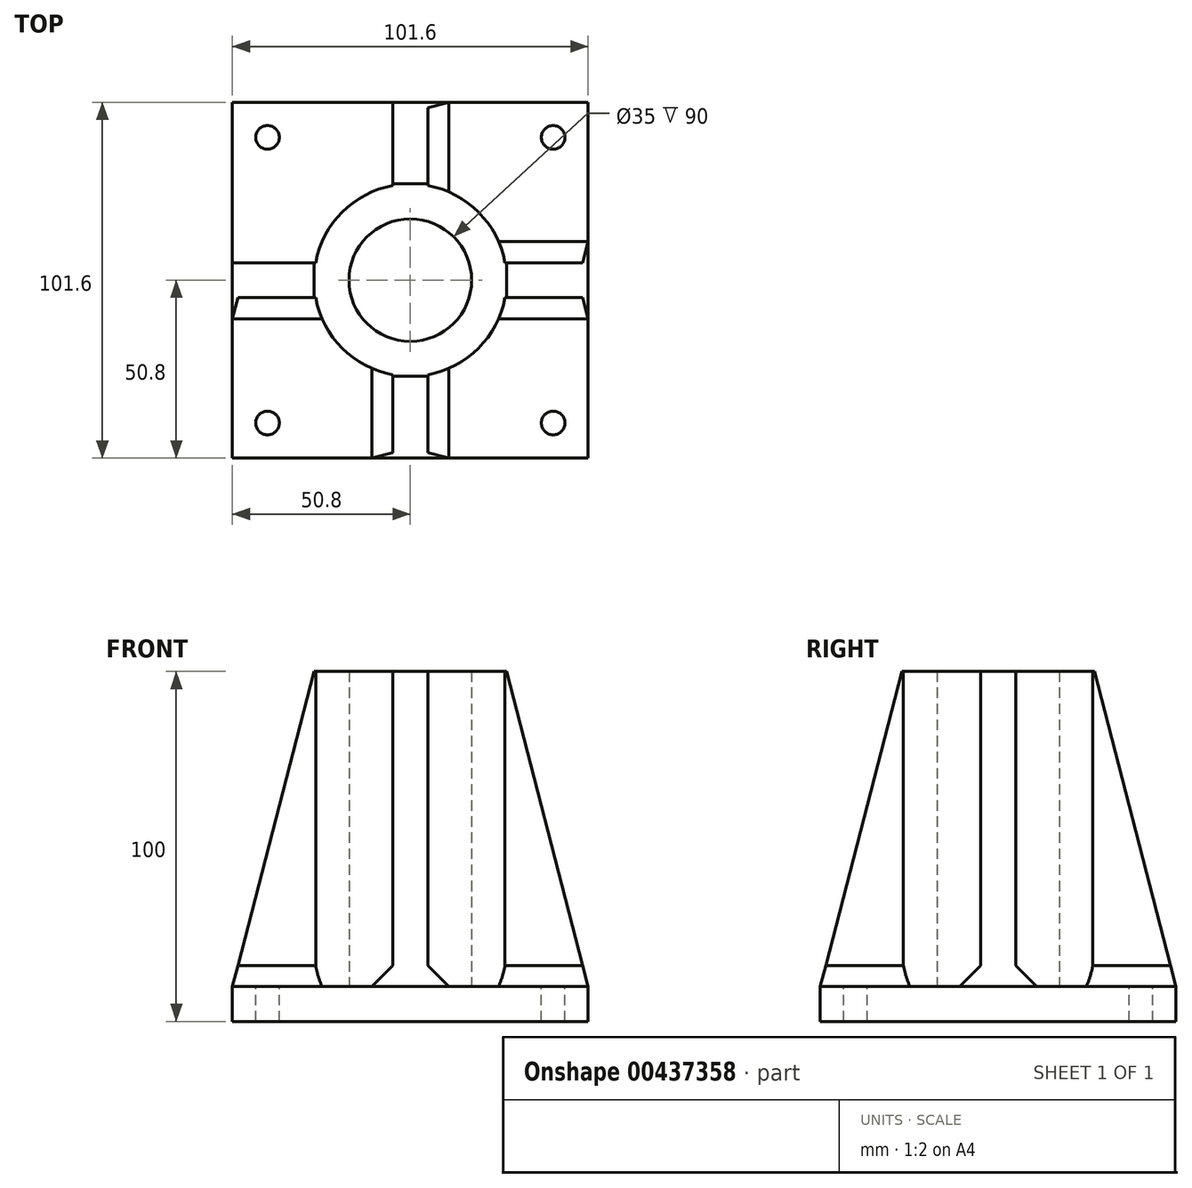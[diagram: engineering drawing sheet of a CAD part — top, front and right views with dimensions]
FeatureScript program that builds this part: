
annotation { "Feature Type Name" : "Feature", "Feature Type Description" : "" }
export const myFeature = defineFeature(function(context is Context, id is Id, definition is map)
    precondition{}
    {
        {
            assignVariable(context, id + "F0", {"name" : "PrintingOffset", "anyValue" : .5});
        }
        {
            assignVariable(context, id + "F1", {"name" : "BoltHoleDiameter", "anyValue" : 6.25 + getVariable(context, 'PrintingOffset')});
        }
        {
            assignVariable(context, id + "F2", {"name" : "PlateLength", "anyValue" : 101.6});
        }
        {
            assignVariable(context, id + "F3", {"name" : "PlateWidth", "anyValue" : getVariable(context, 'PlateLength')});
        }
        {
            assignVariable(context, id + "F4", {"name" : "TableLegDiameter", "anyValue" : 34.5 + getVariable(context, 'PrintingOffset')});
        }
        {
            assignVariable(context, id + "F5", {"name" : "WallThickness", "anyValue" : 10});
        }
        {
            var Q0;
            Q0=qCreatedBy(makeId("Top.planeOp"),FACE);
            var sketch = newSketch(context, id + "F6", { "sketchPlane" : qUnion([Q0])});
            skLineSegment(sketch, "E0.rect.bottom", {"start": v(50.8, 50.8) * mm, "end": v(-50.8, 50.8) * mm});
            skLineSegment(sketch, "E0.rect.top", {"start": v(50.8, -50.8) * mm, "end": v(-50.8, -50.8) * mm});
            skLineSegment(sketch, "E0.rect.left", {"start": v(50.8, 50.8) * mm, "end": v(50.8, -50.8) * mm});
            skLineSegment(sketch, "E0.rect.right", {"start": v(-50.8, 50.8) * mm, "end": v(-50.8, -50.8) * mm});
            skPoint(sketch, "E0.rect.middle", {"position": v(0, 0) * mm});
            skCircle(sketch, "E1", {"center": v(0, 0) * mm, "radius": 17.5 * mm});
            skLineSegment(sketch, "E2", {"start": v(0, 50.8) * mm, "end": v(0, -50.8) * mm, "construction": true});
            skLineSegment(sketch, "E3", {"start": v(-50.8, 0) * mm, "end": v(50.8, 0) * mm, "construction": true});
            skCircle(sketch, "E4.0", {"center": v(0, 0) * mm, "radius": 27.5 * mm});
            skLineSegment(sketch, "E5.3.0", {"start": v(-27.04, 5) * mm, "end": v(-50.8, 5) * mm});
            skLineSegment(sketch, "E5.3.1", {"start": v(-27.04, -5) * mm, "end": v(-50.8, -5) * mm});
            skPoint(sketch, "E6", {"position": v(-40.8, 40.8) * mm});
            skLineSegment(sketch, "E7", {"start": v(0, -17.5) * mm, "end": v(0, -17.5) * mm});
            skLineSegment(sketch, "E8.1.0", {"start": v(1.46, -17.44) * mm, "end": v(1.46, -17.44) * mm});
            skLineSegment(sketch, "E8.2.0", {"start": v(2.92, -17.25) * mm, "end": v(2.92, -17.25) * mm});
            skLineSegment(sketch, "E8.3.0", {"start": v(4.35, -16.95) * mm, "end": v(4.35, -16.95) * mm});
            skLineSegment(sketch, "E8.4.0", {"start": v(5.76, -16.53) * mm, "end": v(5.76, -16.53) * mm});
            skLineSegment(sketch, "E8.5.0", {"start": v(7.12, -15.99) * mm, "end": v(7.12, -15.99) * mm});
            skLineSegment(sketch, "E8.6.0", {"start": v(8.43, -15.34) * mm, "end": v(8.43, -15.34) * mm});
            skLineSegment(sketch, "E8.7.0", {"start": v(9.68, -14.58) * mm, "end": v(9.68, -14.58) * mm});
            skLineSegment(sketch, "E8.8.0", {"start": v(10.87, -13.71) * mm, "end": v(10.87, -13.71) * mm});
            skLineSegment(sketch, "E8.9.0", {"start": v(11.98, -12.76) * mm, "end": v(11.98, -12.76) * mm});
            skLineSegment(sketch, "E8.10.0", {"start": v(13, -11.7) * mm, "end": v(13, -11.7) * mm});
            skLineSegment(sketch, "E8.11.0", {"start": v(13.94, -10.58) * mm, "end": v(13.94, -10.58) * mm});
            skLineSegment(sketch, "E8.12.0", {"start": v(14.78, -9.38) * mm, "end": v(14.78, -9.38) * mm});
            skLineSegment(sketch, "E8.13.0", {"start": v(15.5, -8.1) * mm, "end": v(15.5, -8.1) * mm});
            skLineSegment(sketch, "E8.14.0", {"start": v(16.13, -6.78) * mm, "end": v(16.13, -6.78) * mm});
            skLineSegment(sketch, "E8.15.0", {"start": v(16.64, -5.4) * mm, "end": v(16.64, -5.4) * mm});
            skLineSegment(sketch, "E8.16.0", {"start": v(17.04, -4) * mm, "end": v(17.04, -4) * mm});
            skLineSegment(sketch, "E8.17.0", {"start": v(17.31, -2.56) * mm, "end": v(17.31, -2.56) * mm});
            skLineSegment(sketch, "E8.18.0", {"start": v(17.47, -1.1) * mm, "end": v(17.47, -1.1) * mm});
            skLineSegment(sketch, "E8.19.0", {"start": v(17.5, 0.37) * mm, "end": v(17.5, 0.37) * mm});
            skLineSegment(sketch, "E8.20.0", {"start": v(17.4, 1.83) * mm, "end": v(17.4, 1.83) * mm});
            skLineSegment(sketch, "E8.21.0", {"start": v(17.2, 3.28) * mm, "end": v(17.2, 3.28) * mm});
            skLineSegment(sketch, "E8.22.0", {"start": v(16.86, 4.7) * mm, "end": v(16.86, 4.7) * mm});
            skLineSegment(sketch, "E8.23.0", {"start": v(16.4, 6.1) * mm, "end": v(16.4, 6.1) * mm});
            skLineSegment(sketch, "E8.24.0", {"start": v(15.83, 7.45) * mm, "end": v(15.83, 7.45) * mm});
            skLineSegment(sketch, "E8.25.0", {"start": v(15.16, 8.75) * mm, "end": v(15.16, 8.75) * mm});
            skLineSegment(sketch, "E8.26.0", {"start": v(14.37, 9.99) * mm, "end": v(14.37, 9.99) * mm});
            skLineSegment(sketch, "E8.27.0", {"start": v(13.48, 11.15) * mm, "end": v(13.48, 11.15) * mm});
            skLineSegment(sketch, "E8.28.0", {"start": v(12.5, 12.24) * mm, "end": v(12.5, 12.24) * mm});
            skLineSegment(sketch, "E8.29.0", {"start": v(11.43, 13.25) * mm, "end": v(11.43, 13.25) * mm});
            skLineSegment(sketch, "E8.30.0", {"start": v(10.29, 14.16) * mm, "end": v(10.29, 14.16) * mm});
            skLineSegment(sketch, "E8.31.0", {"start": v(9.07, 14.97) * mm, "end": v(9.07, 14.97) * mm});
            skLineSegment(sketch, "E8.32.0", {"start": v(7.78, 15.67) * mm, "end": v(7.78, 15.67) * mm});
            skLineSegment(sketch, "E8.33.0", {"start": v(6.44, 16.27) * mm, "end": v(6.44, 16.27) * mm});
            skLineSegment(sketch, "E8.34.0", {"start": v(5.06, 16.75) * mm, "end": v(5.06, 16.75) * mm});
            skLineSegment(sketch, "E8.35.0", {"start": v(3.64, 17.12) * mm, "end": v(3.64, 17.12) * mm});
            skLineSegment(sketch, "E8.36.0", {"start": v(2.2, 17.36) * mm, "end": v(2.2, 17.36) * mm});
            skLineSegment(sketch, "E8.37.0", {"start": v(0.73, 17.48) * mm, "end": v(0.73, 17.48) * mm});
            skLineSegment(sketch, "E8.38.0", {"start": v(-0.73, 17.48) * mm, "end": v(-0.73, 17.48) * mm});
            skLineSegment(sketch, "E8.39.0", {"start": v(-2.2, 17.36) * mm, "end": v(-2.2, 17.36) * mm});
            skLineSegment(sketch, "E8.40.0", {"start": v(-3.64, 17.12) * mm, "end": v(-3.64, 17.12) * mm});
            skLineSegment(sketch, "E8.41.0", {"start": v(-5.06, 16.75) * mm, "end": v(-5.06, 16.75) * mm});
            skLineSegment(sketch, "E8.42.0", {"start": v(-6.44, 16.27) * mm, "end": v(-6.44, 16.27) * mm});
            skLineSegment(sketch, "E8.43.0", {"start": v(-7.78, 15.67) * mm, "end": v(-7.78, 15.67) * mm});
            skLineSegment(sketch, "E8.44.0", {"start": v(-9.07, 14.97) * mm, "end": v(-9.07, 14.97) * mm});
            skLineSegment(sketch, "E8.45.0", {"start": v(-10.29, 14.16) * mm, "end": v(-10.29, 14.16) * mm});
            skLineSegment(sketch, "E8.46.0", {"start": v(-11.43, 13.25) * mm, "end": v(-11.43, 13.25) * mm});
            skLineSegment(sketch, "E8.47.0", {"start": v(-12.5, 12.24) * mm, "end": v(-12.5, 12.24) * mm});
            skLineSegment(sketch, "E8.48.0", {"start": v(-13.48, 11.15) * mm, "end": v(-13.48, 11.15) * mm});
            skLineSegment(sketch, "E8.49.0", {"start": v(-14.37, 9.99) * mm, "end": v(-14.37, 9.99) * mm});
            skLineSegment(sketch, "E8.50.0", {"start": v(-15.16, 8.75) * mm, "end": v(-15.16, 8.75) * mm});
            skLineSegment(sketch, "E8.51.0", {"start": v(-15.83, 7.45) * mm, "end": v(-15.83, 7.45) * mm});
            skLineSegment(sketch, "E8.52.0", {"start": v(-16.4, 6.1) * mm, "end": v(-16.4, 6.1) * mm});
            skLineSegment(sketch, "E8.53.0", {"start": v(-16.86, 4.7) * mm, "end": v(-16.86, 4.7) * mm});
            skLineSegment(sketch, "E8.54.0", {"start": v(-17.2, 3.28) * mm, "end": v(-17.2, 3.28) * mm});
            skLineSegment(sketch, "E8.55.0", {"start": v(-17.4, 1.83) * mm, "end": v(-17.4, 1.83) * mm});
            skLineSegment(sketch, "E8.56.0", {"start": v(-17.5, 0.37) * mm, "end": v(-17.5, 0.37) * mm});
            skLineSegment(sketch, "E8.57.0", {"start": v(-17.47, -1.1) * mm, "end": v(-17.47, -1.1) * mm});
            skLineSegment(sketch, "E8.58.0", {"start": v(-17.31, -2.56) * mm, "end": v(-17.31, -2.56) * mm});
            skLineSegment(sketch, "E8.59.0", {"start": v(-17.04, -4) * mm, "end": v(-17.04, -4) * mm});
            skLineSegment(sketch, "E8.60.0", {"start": v(-16.64, -5.4) * mm, "end": v(-16.64, -5.4) * mm});
            skLineSegment(sketch, "E8.61.0", {"start": v(-16.13, -6.78) * mm, "end": v(-16.13, -6.78) * mm});
            skLineSegment(sketch, "E8.62.0", {"start": v(-15.5, -8.1) * mm, "end": v(-15.5, -8.1) * mm});
            skLineSegment(sketch, "E8.63.0", {"start": v(-14.78, -9.38) * mm, "end": v(-14.78, -9.38) * mm});
            skLineSegment(sketch, "E8.64.0", {"start": v(-13.94, -10.58) * mm, "end": v(-13.94, -10.58) * mm});
            skLineSegment(sketch, "E8.65.0", {"start": v(-13, -11.7) * mm, "end": v(-13, -11.7) * mm});
            skLineSegment(sketch, "E8.66.0", {"start": v(-11.98, -12.76) * mm, "end": v(-11.98, -12.76) * mm});
            skLineSegment(sketch, "E8.67.0", {"start": v(-10.87, -13.71) * mm, "end": v(-10.87, -13.71) * mm});
            skLineSegment(sketch, "E8.68.0", {"start": v(-9.68, -14.58) * mm, "end": v(-9.68, -14.58) * mm});
            skLineSegment(sketch, "E8.69.0", {"start": v(-8.43, -15.34) * mm, "end": v(-8.43, -15.34) * mm});
            skLineSegment(sketch, "E9.2.70.0", {"start": v(-7.12, -15.99) * mm, "end": v(-7.12, -15.99) * mm});
            skLineSegment(sketch, "E9.2.71.0", {"start": v(-5.76, -16.53) * mm, "end": v(-5.76, -16.53) * mm});
            skLineSegment(sketch, "E9.2.72.0", {"start": v(-4.35, -16.95) * mm, "end": v(-4.35, -16.95) * mm});
            skLineSegment(sketch, "E9.2.73.0", {"start": v(-2.92, -17.25) * mm, "end": v(-2.92, -17.25) * mm});
            skLineSegment(sketch, "E9.2.74.0", {"start": v(-1.46, -17.44) * mm, "end": v(-1.46, -17.44) * mm});
            skLineSegment(sketch, "E10.MirrorCS", {"start": v(27.04, -5) * mm, "end": v(50.8, -5) * mm});
            skLineSegment(sketch, "E11.MirrorCS", {"start": v(27.04, 5) * mm, "end": v(50.8, 5) * mm});
            skLineSegment(sketch, "E12.MirrorCS", {"start": v(-5, 27.04) * mm, "end": v(-5, 50.8) * mm});
            skLineSegment(sketch, "E13.MirrorCS", {"start": v(5, 27.04) * mm, "end": v(5, 50.8) * mm});
            skLineSegment(sketch, "E14.MirrorCS", {"start": v(-5, -27.04) * mm, "end": v(-5, -50.8) * mm});
            skLineSegment(sketch, "E15.MirrorCS", {"start": v(5, -27.04) * mm, "end": v(5, -50.8) * mm});
            skPoint(sketch, "E16.MirrorP", {"position": v(-40.8, -40.8) * mm});
            skPoint(sketch, "E17.MirrorP", {"position": v(40.8, 40.8) * mm});
            skPoint(sketch, "E18.MirrorP", {"position": v(40.8, -40.8) * mm});
            skSolve(sketch);
        }
        {
            assignVariable(context, id + "F7", {"name" : "CylinderHeight", "anyValue" : 90});
        }
        {
            var Q0;
            Q0=makeQuery(id+"F6.imprint","IMPRINT",FACE,{"disambiguationData":[TD([[makeQuery(id+"F6.imprint","IMPRINT",EDGE,{"derivedFrom":sQuery(id+"F6.wireOp",EDGE,"E1")}),-1.0]])]});
            extrude(context, id + "F8", {"entities" : qUnion([Q0]), "depth" : (getVariable(context, 'CylinderHeight')) * mm});
        }
        {
            var Q0;
            {var subQ1=sQuery(id+"F6.wireOp",EDGE,"E5.3.0");Q0=makeQuery(id+"F6.imprint","IMPRINT",FACE,{"disambiguationData":[TD([[makeQuery(id+"F6.imprint","IMPRINT",EDGE,{"derivedFrom":subQ1}),1.0]])]});}
            var Q1;
            {var subQ2=sQuery(id+"F6.wireOp",EDGE,"E5.1.1");Q1=makeQuery(id+"F6.imprint","IMPRINT",FACE,{"disambiguationData":[TD([[makeQuery(id+"F6.imprint","IMPRINT",EDGE,{"derivedFrom":subQ2}),1.0]])]});}
            var Q2;
            {var subQ0=sQuery(id+"F6.wireOp",EDGE,"E1");var subQ1=sQuery(id+"F6.wireOp",EDGE,"E8.25.0");var subQ174=makeQuery(id+"F6.imprint","INTERSECT",VERTEX,{"disambiguationData":[OD(1.0)],"derivedFrom":[subQ0,subQ1]});Q2=makeQuery(id+"F6.imprint","IMPRINT",FACE,{"disambiguationData":[TD([[makeQuery(id+"F6.imprint","IMPRINT",EDGE,{"disambiguationData":[TD([[subQ174,-1.0]])],"derivedFrom":subQ0}),1.0]])]});}
            var Q3;
            {var subQ0=sQuery(id+"F6.wireOp",EDGE,"E5.1.0");Q3=makeQuery(id+"F6.imprint","IMPRINT",FACE,{"disambiguationData":[TD([[makeQuery(id+"F6.imprint","IMPRINT",EDGE,{"derivedFrom":subQ0}),1.0]])]});}
            var Q4;
            {var subQ86=sQuery(id+"F6.wireOp",EDGE,"E7");Q4=makeQuery(id+"F6.imprint","IMPRINT",FACE,{"disambiguationData":[TD([[makeQuery(id+"F6.imprint","IMPRINT",EDGE,{"derivedFrom":subQ86}),-1.0]])]});}
            var Q5;
            {var subQ1=sQuery(id+"F6.wireOp",EDGE,"E5.2.0");Q5=makeQuery(id+"F6.imprint","IMPRINT",FACE,{"disambiguationData":[TD([[makeQuery(id+"F6.imprint","IMPRINT",EDGE,{"derivedFrom":subQ1}),1.0]])]});}
            var Q6;
            {var subQ1=sQuery(id+"F6.wireOp",EDGE,"E5.2.1");Q6=makeQuery(id+"F6.imprint","IMPRINT",FACE,{"disambiguationData":[TD([[makeQuery(id+"F6.imprint","IMPRINT",EDGE,{"derivedFrom":subQ1}),1.0]])]});}
            var Q7;
            {var subQ0=sQuery(id+"F6.wireOp",EDGE,"108301c5-a481-47a9-95d8-fa25c03050fa");Q7=makeQuery(id+"F6.imprint","IMPRINT",FACE,{"disambiguationData":[TD([[makeQuery(id+"F6.imprint","IMPRINT",EDGE,{"derivedFrom":subQ0}),1.0]])]});}
            var Q8;
            {var subQ1=sQuery(id+"F6.wireOp",EDGE,"79e71fa4-d721-44c3-a3e5-dd1a67dfb6ba");Q8=makeQuery(id+"F6.imprint","IMPRINT",FACE,{"disambiguationData":[TD([[makeQuery(id+"F6.imprint","IMPRINT",EDGE,{"derivedFrom":subQ1}),1.0]])]});}
            var Q9;
            {var subQ1=sQuery(id+"F6.wireOp",EDGE,"79e71fa4-d721-44c3-a3e5-dd1a67dfb6ba");Q9=makeQuery(id+"F6.imprint","IMPRINT",FACE,{"disambiguationData":[TD([[makeQuery(id+"F6.imprint","IMPRINT",EDGE,{"derivedFrom":subQ1}),-1.0]])]});}
            var Q10;
            Q10=makeQuery(id+"F8.opExtrude","CAP_FACE",FACE,{"disambiguationData":[OSD([sQuery(id+"F6.wireOp",EDGE,"E1"),sQuery(id+"F6.wireOp",EDGE,"E4.0"),sQuery(id+"F6.wireOp",EDGE,"E7"),sQuery(id+"F6.wireOp",EDGE,"E8.1.0"),sQuery(id+"F6.wireOp",EDGE,"E8.2.0"),sQuery(id+"F6.wireOp",EDGE,"E8.3.0"),sQuery(id+"F6.wireOp",EDGE,"E8.4.0"),sQuery(id+"F6.wireOp",EDGE,"E8.5.0"),sQuery(id+"F6.wireOp",EDGE,"E8.6.0"),sQuery(id+"F6.wireOp",EDGE,"E8.7.0"),sQuery(id+"F6.wireOp",EDGE,"E8.8.0"),sQuery(id+"F6.wireOp",EDGE,"E8.9.0"),sQuery(id+"F6.wireOp",EDGE,"E8.10.0"),sQuery(id+"F6.wireOp",EDGE,"E8.11.0"),sQuery(id+"F6.wireOp",EDGE,"E8.12.0"),sQuery(id+"F6.wireOp",EDGE,"E8.13.0"),sQuery(id+"F6.wireOp",EDGE,"E8.14.0"),sQuery(id+"F6.wireOp",EDGE,"E8.15.0"),sQuery(id+"F6.wireOp",EDGE,"E8.16.0"),sQuery(id+"F6.wireOp",EDGE,"E8.17.0"),sQuery(id+"F6.wireOp",EDGE,"E8.18.0"),sQuery(id+"F6.wireOp",EDGE,"E8.19.0"),sQuery(id+"F6.wireOp",EDGE,"E8.20.0"),sQuery(id+"F6.wireOp",EDGE,"E8.21.0"),sQuery(id+"F6.wireOp",EDGE,"E8.22.0"),sQuery(id+"F6.wireOp",EDGE,"E8.23.0"),sQuery(id+"F6.wireOp",EDGE,"E8.24.0"),sQuery(id+"F6.wireOp",EDGE,"E8.25.0"),sQuery(id+"F6.wireOp",EDGE,"E8.26.0"),sQuery(id+"F6.wireOp",EDGE,"E8.27.0"),sQuery(id+"F6.wireOp",EDGE,"E8.28.0"),sQuery(id+"F6.wireOp",EDGE,"E8.29.0"),sQuery(id+"F6.wireOp",EDGE,"E8.30.0"),sQuery(id+"F6.wireOp",EDGE,"E8.31.0"),sQuery(id+"F6.wireOp",EDGE,"E8.32.0"),sQuery(id+"F6.wireOp",EDGE,"E8.33.0"),sQuery(id+"F6.wireOp",EDGE,"E8.34.0"),sQuery(id+"F6.wireOp",EDGE,"E8.35.0"),sQuery(id+"F6.wireOp",EDGE,"E8.36.0"),sQuery(id+"F6.wireOp",EDGE,"E8.37.0"),sQuery(id+"F6.wireOp",EDGE,"E8.38.0"),sQuery(id+"F6.wireOp",EDGE,"E8.39.0"),sQuery(id+"F6.wireOp",EDGE,"E8.40.0"),sQuery(id+"F6.wireOp",EDGE,"E8.41.0"),sQuery(id+"F6.wireOp",EDGE,"E8.42.0"),sQuery(id+"F6.wireOp",EDGE,"E8.43.0"),sQuery(id+"F6.wireOp",EDGE,"E8.44.0"),sQuery(id+"F6.wireOp",EDGE,"E8.45.0"),sQuery(id+"F6.wireOp",EDGE,"E8.46.0"),sQuery(id+"F6.wireOp",EDGE,"E8.47.0"),sQuery(id+"F6.wireOp",EDGE,"E8.48.0"),sQuery(id+"F6.wireOp",EDGE,"E8.49.0"),sQuery(id+"F6.wireOp",EDGE,"E8.50.0"),sQuery(id+"F6.wireOp",EDGE,"E8.51.0"),sQuery(id+"F6.wireOp",EDGE,"E8.52.0"),sQuery(id+"F6.wireOp",EDGE,"E8.53.0"),sQuery(id+"F6.wireOp",EDGE,"E8.54.0"),sQuery(id+"F6.wireOp",EDGE,"E8.55.0"),sQuery(id+"F6.wireOp",EDGE,"E8.56.0"),sQuery(id+"F6.wireOp",EDGE,"E8.57.0"),sQuery(id+"F6.wireOp",EDGE,"E8.58.0"),sQuery(id+"F6.wireOp",EDGE,"E8.59.0"),sQuery(id+"F6.wireOp",EDGE,"E8.60.0"),sQuery(id+"F6.wireOp",EDGE,"E8.61.0"),sQuery(id+"F6.wireOp",EDGE,"E8.62.0"),sQuery(id+"F6.wireOp",EDGE,"E8.63.0"),sQuery(id+"F6.wireOp",EDGE,"E8.64.0"),sQuery(id+"F6.wireOp",EDGE,"E8.65.0"),sQuery(id+"F6.wireOp",EDGE,"E8.66.0"),sQuery(id+"F6.wireOp",EDGE,"E8.67.0"),sQuery(id+"F6.wireOp",EDGE,"E8.68.0"),sQuery(id+"F6.wireOp",EDGE,"E8.69.0"),sQuery(id+"F6.wireOp",EDGE,"E8.70.0"),sQuery(id+"F6.wireOp",EDGE,"E8.71.0"),sQuery(id+"F6.wireOp",EDGE,"E8.72.0"),sQuery(id+"F6.wireOp",EDGE,"E8.73.0"),sQuery(id+"F6.wireOp",EDGE,"E8.74.0"),sQuery(id+"F6.wireOp",EDGE,"E8.75.0"),sQuery(id+"F6.wireOp",EDGE,"E8.76.0"),sQuery(id+"F6.wireOp",EDGE,"E8.77.0"),sQuery(id+"F6.wireOp",EDGE,"E8.78.0"),sQuery(id+"F6.wireOp",EDGE,"E8.79.0"),sQuery(id+"F6.wireOp",EDGE,"E8.80.0"),sQuery(id+"F6.wireOp",EDGE,"E8.81.0"),sQuery(id+"F6.wireOp",EDGE,"E8.82.0"),sQuery(id+"F6.wireOp",EDGE,"E8.83.0"),sQuery(id+"F6.wireOp",EDGE,"E8.84.0"),sQuery(id+"F6.wireOp",EDGE,"E8.85.0"),sQuery(id+"F6.wireOp",EDGE,"E8.86.0"),sQuery(id+"F6.wireOp",EDGE,"E8.87.0"),sQuery(id+"F6.wireOp",EDGE,"E8.88.0"),sQuery(id+"F6.wireOp",EDGE,"E8.89.0"),sQuery(id+"F6.wireOp",EDGE,"E8.90.0"),sQuery(id+"F6.wireOp",EDGE,"E8.91.0"),sQuery(id+"F6.wireOp",EDGE,"E8.92.0"),sQuery(id+"F6.wireOp",EDGE,"E8.93.0"),sQuery(id+"F6.wireOp",EDGE,"E8.94.0"),sQuery(id+"F6.wireOp",EDGE,"E8.95.0"),sQuery(id+"F6.wireOp",EDGE,"E8.96.0"),sQuery(id+"F6.wireOp",EDGE,"E8.97.0"),sQuery(id+"F6.wireOp",EDGE,"E8.98.0"),sQuery(id+"F6.wireOp",EDGE,"E8.99.0")])],"isStart":true});
            var Q11;
            Q11=makeQuery(id+"F8.opExtrude","CAP_FACE",FACE,{"disambiguationData":[OSD([sQuery(id+"F6.wireOp",EDGE,"E1"),sQuery(id+"F6.wireOp",EDGE,"E4.0"),sQuery(id+"F6.wireOp",EDGE,"E7"),sQuery(id+"F6.wireOp",EDGE,"E8.1.0"),sQuery(id+"F6.wireOp",EDGE,"E8.2.0"),sQuery(id+"F6.wireOp",EDGE,"E8.3.0"),sQuery(id+"F6.wireOp",EDGE,"E8.4.0"),sQuery(id+"F6.wireOp",EDGE,"E8.5.0"),sQuery(id+"F6.wireOp",EDGE,"E8.6.0"),sQuery(id+"F6.wireOp",EDGE,"E8.7.0"),sQuery(id+"F6.wireOp",EDGE,"E8.8.0"),sQuery(id+"F6.wireOp",EDGE,"E8.9.0"),sQuery(id+"F6.wireOp",EDGE,"E8.10.0"),sQuery(id+"F6.wireOp",EDGE,"E8.11.0"),sQuery(id+"F6.wireOp",EDGE,"E8.12.0"),sQuery(id+"F6.wireOp",EDGE,"E8.13.0"),sQuery(id+"F6.wireOp",EDGE,"E8.14.0"),sQuery(id+"F6.wireOp",EDGE,"E8.15.0"),sQuery(id+"F6.wireOp",EDGE,"E8.16.0"),sQuery(id+"F6.wireOp",EDGE,"E8.17.0"),sQuery(id+"F6.wireOp",EDGE,"E8.18.0"),sQuery(id+"F6.wireOp",EDGE,"E8.19.0"),sQuery(id+"F6.wireOp",EDGE,"E8.20.0"),sQuery(id+"F6.wireOp",EDGE,"E8.21.0"),sQuery(id+"F6.wireOp",EDGE,"E8.22.0"),sQuery(id+"F6.wireOp",EDGE,"E8.23.0"),sQuery(id+"F6.wireOp",EDGE,"E8.24.0"),sQuery(id+"F6.wireOp",EDGE,"E8.25.0"),sQuery(id+"F6.wireOp",EDGE,"E8.26.0"),sQuery(id+"F6.wireOp",EDGE,"E8.27.0"),sQuery(id+"F6.wireOp",EDGE,"E8.28.0"),sQuery(id+"F6.wireOp",EDGE,"E8.29.0"),sQuery(id+"F6.wireOp",EDGE,"E8.30.0"),sQuery(id+"F6.wireOp",EDGE,"E8.31.0"),sQuery(id+"F6.wireOp",EDGE,"E8.32.0"),sQuery(id+"F6.wireOp",EDGE,"E8.33.0"),sQuery(id+"F6.wireOp",EDGE,"E8.34.0"),sQuery(id+"F6.wireOp",EDGE,"E8.35.0"),sQuery(id+"F6.wireOp",EDGE,"E8.36.0"),sQuery(id+"F6.wireOp",EDGE,"E8.37.0"),sQuery(id+"F6.wireOp",EDGE,"E8.38.0"),sQuery(id+"F6.wireOp",EDGE,"E8.39.0"),sQuery(id+"F6.wireOp",EDGE,"E8.40.0"),sQuery(id+"F6.wireOp",EDGE,"E8.41.0"),sQuery(id+"F6.wireOp",EDGE,"E8.42.0"),sQuery(id+"F6.wireOp",EDGE,"E8.43.0"),sQuery(id+"F6.wireOp",EDGE,"E8.44.0"),sQuery(id+"F6.wireOp",EDGE,"E8.45.0"),sQuery(id+"F6.wireOp",EDGE,"E8.46.0"),sQuery(id+"F6.wireOp",EDGE,"E8.47.0"),sQuery(id+"F6.wireOp",EDGE,"E8.48.0"),sQuery(id+"F6.wireOp",EDGE,"E8.49.0"),sQuery(id+"F6.wireOp",EDGE,"E8.50.0"),sQuery(id+"F6.wireOp",EDGE,"E8.51.0"),sQuery(id+"F6.wireOp",EDGE,"E8.52.0"),sQuery(id+"F6.wireOp",EDGE,"E8.53.0"),sQuery(id+"F6.wireOp",EDGE,"E8.54.0"),sQuery(id+"F6.wireOp",EDGE,"E8.55.0"),sQuery(id+"F6.wireOp",EDGE,"E8.56.0"),sQuery(id+"F6.wireOp",EDGE,"E8.57.0"),sQuery(id+"F6.wireOp",EDGE,"E8.58.0"),sQuery(id+"F6.wireOp",EDGE,"E8.59.0"),sQuery(id+"F6.wireOp",EDGE,"E8.60.0"),sQuery(id+"F6.wireOp",EDGE,"E8.61.0"),sQuery(id+"F6.wireOp",EDGE,"E8.62.0"),sQuery(id+"F6.wireOp",EDGE,"E8.63.0"),sQuery(id+"F6.wireOp",EDGE,"E8.64.0"),sQuery(id+"F6.wireOp",EDGE,"E8.65.0"),sQuery(id+"F6.wireOp",EDGE,"E8.66.0"),sQuery(id+"F6.wireOp",EDGE,"E8.67.0"),sQuery(id+"F6.wireOp",EDGE,"E8.68.0"),sQuery(id+"F6.wireOp",EDGE,"E8.69.0"),sQuery(id+"F6.wireOp",EDGE,"E8.70.0"),sQuery(id+"F6.wireOp",EDGE,"E8.71.0"),sQuery(id+"F6.wireOp",EDGE,"E8.72.0"),sQuery(id+"F6.wireOp",EDGE,"E8.73.0"),sQuery(id+"F6.wireOp",EDGE,"E8.74.0"),sQuery(id+"F6.wireOp",EDGE,"E8.75.0"),sQuery(id+"F6.wireOp",EDGE,"E8.76.0"),sQuery(id+"F6.wireOp",EDGE,"E8.77.0"),sQuery(id+"F6.wireOp",EDGE,"E8.78.0"),sQuery(id+"F6.wireOp",EDGE,"E8.79.0"),sQuery(id+"F6.wireOp",EDGE,"E8.80.0"),sQuery(id+"F6.wireOp",EDGE,"E8.81.0"),sQuery(id+"F6.wireOp",EDGE,"E8.82.0"),sQuery(id+"F6.wireOp",EDGE,"E8.83.0"),sQuery(id+"F6.wireOp",EDGE,"E8.84.0"),sQuery(id+"F6.wireOp",EDGE,"E8.85.0"),sQuery(id+"F6.wireOp",EDGE,"E8.86.0"),sQuery(id+"F6.wireOp",EDGE,"E8.87.0"),sQuery(id+"F6.wireOp",EDGE,"E8.88.0"),sQuery(id+"F6.wireOp",EDGE,"E8.89.0"),sQuery(id+"F6.wireOp",EDGE,"E8.90.0"),sQuery(id+"F6.wireOp",EDGE,"E8.91.0"),sQuery(id+"F6.wireOp",EDGE,"E8.92.0"),sQuery(id+"F6.wireOp",EDGE,"E8.93.0"),sQuery(id+"F6.wireOp",EDGE,"E8.94.0"),sQuery(id+"F6.wireOp",EDGE,"E8.95.0"),sQuery(id+"F6.wireOp",EDGE,"E8.96.0"),sQuery(id+"F6.wireOp",EDGE,"E8.97.0"),sQuery(id+"F6.wireOp",EDGE,"E8.98.0"),sQuery(id+"F6.wireOp",EDGE,"E8.99.0")])],"isStart":false});
            var Q12;
            {var subQ0=sQuery(id+"F6.wireOp",EDGE,"E8.86.0");Q12=makeQuery(id+"F6.imprint","IMPRINT",FACE,{"disambiguationData":[TD([[makeQuery(id+"F6.imprint","IMPRINT",EDGE,{"derivedFrom":subQ0}),1.0]])]});}
            var Q13;
            {var subQ0=sQuery(id+"F6.wireOp",EDGE,"E8.79.0");Q13=makeQuery(id+"F6.imprint","IMPRINT",FACE,{"disambiguationData":[TD([[makeQuery(id+"F6.imprint","IMPRINT",EDGE,{"derivedFrom":subQ0}),1.0]])]});}
            var Q14;
            {var subQ0=sQuery(id+"F6.wireOp",EDGE,"E8.31.0");Q14=makeQuery(id+"F6.imprint","IMPRINT",FACE,{"disambiguationData":[TD([[makeQuery(id+"F6.imprint","IMPRINT",EDGE,{"derivedFrom":subQ0}),1.0]])]});}
            var Q15;
            {var subQ0=sQuery(id+"F6.wireOp",EDGE,"E8.32.0");Q15=makeQuery(id+"F6.imprint","IMPRINT",FACE,{"disambiguationData":[TD([[makeQuery(id+"F6.imprint","IMPRINT",EDGE,{"derivedFrom":subQ0}),1.0]])]});}
            var Q16;
            {var subQ0=sQuery(id+"F6.wireOp",EDGE,"E8.21.0");Q16=makeQuery(id+"F6.imprint","IMPRINT",FACE,{"disambiguationData":[TD([[makeQuery(id+"F6.imprint","IMPRINT",EDGE,{"derivedFrom":subQ0}),1.0]])]});}
            var Q17;
            {var subQ0=sQuery(id+"F6.wireOp",EDGE,"E8.71.0");Q17=makeQuery(id+"F6.imprint","IMPRINT",FACE,{"disambiguationData":[TD([[makeQuery(id+"F6.imprint","IMPRINT",EDGE,{"derivedFrom":subQ0}),1.0]])]});}
            var Q18;
            {var subQ0=sQuery(id+"F6.wireOp",EDGE,"E8.78.0");Q18=makeQuery(id+"F6.imprint","IMPRINT",FACE,{"disambiguationData":[TD([[makeQuery(id+"F6.imprint","IMPRINT",EDGE,{"derivedFrom":subQ0}),1.0]])]});}
            var Q19;
            {var subQ0=sQuery(id+"F6.wireOp",EDGE,"E8.25.0");Q19=makeQuery(id+"F6.imprint","IMPRINT",FACE,{"disambiguationData":[TD([[makeQuery(id+"F6.imprint","IMPRINT",EDGE,{"derivedFrom":subQ0}),1.0]])]});}
            var Q20;
            {var subQ0=sQuery(id+"F6.wireOp",EDGE,"E8.61.0");Q20=makeQuery(id+"F6.imprint","IMPRINT",FACE,{"disambiguationData":[TD([[makeQuery(id+"F6.imprint","IMPRINT",EDGE,{"derivedFrom":subQ0}),1.0]])]});}
            var Q21;
            {var subQ0=sQuery(id+"F6.wireOp",EDGE,"E8.45.0");Q21=makeQuery(id+"F6.imprint","IMPRINT",FACE,{"disambiguationData":[TD([[makeQuery(id+"F6.imprint","IMPRINT",EDGE,{"derivedFrom":subQ0}),1.0]])]});}
            var Q22;
            {var subQ0=sQuery(id+"F6.wireOp",EDGE,"E8.10.0");Q22=makeQuery(id+"F6.imprint","IMPRINT",FACE,{"disambiguationData":[TD([[makeQuery(id+"F6.imprint","IMPRINT",EDGE,{"derivedFrom":subQ0}),1.0]])]});}
            var Q23;
            {var subQ0=sQuery(id+"F6.wireOp",EDGE,"E8.7.0");Q23=makeQuery(id+"F6.imprint","IMPRINT",FACE,{"disambiguationData":[TD([[makeQuery(id+"F6.imprint","IMPRINT",EDGE,{"derivedFrom":subQ0}),1.0]])]});}
            var Q24;
            {var subQ0=sQuery(id+"F6.wireOp",EDGE,"E8.43.0");Q24=makeQuery(id+"F6.imprint","IMPRINT",FACE,{"disambiguationData":[TD([[makeQuery(id+"F6.imprint","IMPRINT",EDGE,{"derivedFrom":subQ0}),1.0]])]});}
            var Q25;
            {var subQ0=sQuery(id+"F6.wireOp",EDGE,"E8.22.0");Q25=makeQuery(id+"F6.imprint","IMPRINT",FACE,{"disambiguationData":[TD([[makeQuery(id+"F6.imprint","IMPRINT",EDGE,{"derivedFrom":subQ0}),1.0]])]});}
            var Q26;
            {var subQ0=sQuery(id+"F6.wireOp",EDGE,"E8.90.0");Q26=makeQuery(id+"F6.imprint","IMPRINT",FACE,{"disambiguationData":[TD([[makeQuery(id+"F6.imprint","IMPRINT",EDGE,{"derivedFrom":subQ0}),1.0]])]});}
            var Q27;
            {var subQ0=sQuery(id+"F6.wireOp",EDGE,"E8.58.0");Q27=makeQuery(id+"F6.imprint","IMPRINT",FACE,{"disambiguationData":[TD([[makeQuery(id+"F6.imprint","IMPRINT",EDGE,{"derivedFrom":subQ0}),1.0]])]});}
            var Q28;
            {var subQ0=sQuery(id+"F6.wireOp",EDGE,"E8.70.0");Q28=makeQuery(id+"F6.imprint","IMPRINT",FACE,{"disambiguationData":[TD([[makeQuery(id+"F6.imprint","IMPRINT",EDGE,{"derivedFrom":subQ0}),1.0]])]});}
            var Q29;
            {var subQ0=sQuery(id+"F6.wireOp",EDGE,"E8.20.0");Q29=makeQuery(id+"F6.imprint","IMPRINT",FACE,{"disambiguationData":[TD([[makeQuery(id+"F6.imprint","IMPRINT",EDGE,{"derivedFrom":subQ0}),1.0]])]});}
            var Q30;
            {var subQ0=sQuery(id+"F6.wireOp",EDGE,"E8.72.0");Q30=makeQuery(id+"F6.imprint","IMPRINT",FACE,{"disambiguationData":[TD([[makeQuery(id+"F6.imprint","IMPRINT",EDGE,{"derivedFrom":subQ0}),1.0]])]});}
            var Q31;
            {var subQ0=sQuery(id+"F6.wireOp",EDGE,"E8.88.0");Q31=makeQuery(id+"F6.imprint","IMPRINT",FACE,{"disambiguationData":[TD([[makeQuery(id+"F6.imprint","IMPRINT",EDGE,{"derivedFrom":subQ0}),1.0]])]});}
            var Q32;
            {var subQ0=sQuery(id+"F6.wireOp",EDGE,"E8.17.0");Q32=makeQuery(id+"F6.imprint","IMPRINT",FACE,{"disambiguationData":[TD([[makeQuery(id+"F6.imprint","IMPRINT",EDGE,{"derivedFrom":subQ0}),1.0]])]});}
            var Q33;
            {var subQ0=sQuery(id+"F6.wireOp",EDGE,"E8.69.0");Q33=makeQuery(id+"F6.imprint","IMPRINT",FACE,{"disambiguationData":[TD([[makeQuery(id+"F6.imprint","IMPRINT",EDGE,{"derivedFrom":subQ0}),1.0]])]});}
            var Q34;
            {var subQ0=sQuery(id+"F6.wireOp",EDGE,"E8.19.0");Q34=makeQuery(id+"F6.imprint","IMPRINT",FACE,{"disambiguationData":[TD([[makeQuery(id+"F6.imprint","IMPRINT",EDGE,{"derivedFrom":subQ0}),1.0]])]});}
            var Q35;
            {var subQ0=sQuery(id+"F6.wireOp",EDGE,"E8.85.0");Q35=makeQuery(id+"F6.imprint","IMPRINT",FACE,{"disambiguationData":[TD([[makeQuery(id+"F6.imprint","IMPRINT",EDGE,{"derivedFrom":subQ0}),1.0]])]});}
            var Q36;
            {var subQ0=sQuery(id+"F6.wireOp",EDGE,"E8.24.0");Q36=makeQuery(id+"F6.imprint","IMPRINT",FACE,{"disambiguationData":[TD([[makeQuery(id+"F6.imprint","IMPRINT",EDGE,{"derivedFrom":subQ0}),1.0]])]});}
            var Q37;
            {var subQ0=sQuery(id+"F6.wireOp",EDGE,"E8.23.0");Q37=makeQuery(id+"F6.imprint","IMPRINT",FACE,{"disambiguationData":[TD([[makeQuery(id+"F6.imprint","IMPRINT",EDGE,{"derivedFrom":subQ0}),1.0]])]});}
            var Q38;
            {var subQ0=sQuery(id+"F6.wireOp",EDGE,"E8.56.0");Q38=makeQuery(id+"F6.imprint","IMPRINT",FACE,{"disambiguationData":[TD([[makeQuery(id+"F6.imprint","IMPRINT",EDGE,{"derivedFrom":subQ0}),1.0]])]});}
            var Q39;
            {var subQ0=sQuery(id+"F6.wireOp",EDGE,"E8.95.0");Q39=makeQuery(id+"F6.imprint","IMPRINT",FACE,{"disambiguationData":[TD([[makeQuery(id+"F6.imprint","IMPRINT",EDGE,{"derivedFrom":subQ0}),1.0]])]});}
            var Q40;
            {var subQ0=sQuery(id+"F6.wireOp",EDGE,"E8.47.0");Q40=makeQuery(id+"F6.imprint","IMPRINT",FACE,{"disambiguationData":[TD([[makeQuery(id+"F6.imprint","IMPRINT",EDGE,{"derivedFrom":subQ0}),1.0]])]});}
            var Q41;
            {var subQ0=sQuery(id+"F6.wireOp",EDGE,"E8.12.0");Q41=makeQuery(id+"F6.imprint","IMPRINT",FACE,{"disambiguationData":[TD([[makeQuery(id+"F6.imprint","IMPRINT",EDGE,{"derivedFrom":subQ0}),1.0]])]});}
            var Q42;
            {var subQ0=sQuery(id+"F6.wireOp",EDGE,"E8.96.0");Q42=makeQuery(id+"F6.imprint","IMPRINT",FACE,{"disambiguationData":[TD([[makeQuery(id+"F6.imprint","IMPRINT",EDGE,{"derivedFrom":subQ0}),1.0]])]});}
            var Q43;
            {var subQ0=sQuery(id+"F6.wireOp",EDGE,"E8.48.0");Q43=makeQuery(id+"F6.imprint","IMPRINT",FACE,{"disambiguationData":[TD([[makeQuery(id+"F6.imprint","IMPRINT",EDGE,{"derivedFrom":subQ0}),1.0]])]});}
            var Q44;
            {var subQ0=sQuery(id+"F6.wireOp",EDGE,"E8.26.0");Q44=makeQuery(id+"F6.imprint","IMPRINT",FACE,{"disambiguationData":[TD([[makeQuery(id+"F6.imprint","IMPRINT",EDGE,{"derivedFrom":subQ0}),1.0]])]});}
            var Q45;
            {var subQ0=sQuery(id+"F6.wireOp",EDGE,"E8.27.0");Q45=makeQuery(id+"F6.imprint","IMPRINT",FACE,{"disambiguationData":[TD([[makeQuery(id+"F6.imprint","IMPRINT",EDGE,{"derivedFrom":subQ0}),1.0]])]});}
            var Q46;
            {var subQ0=sQuery(id+"F6.wireOp",EDGE,"E8.28.0");Q46=makeQuery(id+"F6.imprint","IMPRINT",FACE,{"disambiguationData":[TD([[makeQuery(id+"F6.imprint","IMPRINT",EDGE,{"derivedFrom":subQ0}),1.0]])]});}
            var Q47;
            {var subQ0=sQuery(id+"F6.wireOp",EDGE,"E8.29.0");Q47=makeQuery(id+"F6.imprint","IMPRINT",FACE,{"disambiguationData":[TD([[makeQuery(id+"F6.imprint","IMPRINT",EDGE,{"derivedFrom":subQ0}),1.0]])]});}
            var Q48;
            {var subQ0=sQuery(id+"F6.wireOp",EDGE,"E8.33.0");Q48=makeQuery(id+"F6.imprint","IMPRINT",FACE,{"disambiguationData":[TD([[makeQuery(id+"F6.imprint","IMPRINT",EDGE,{"derivedFrom":subQ0}),1.0]])]});}
            var Q49;
            {var subQ0=sQuery(id+"F6.wireOp",EDGE,"E8.34.0");Q49=makeQuery(id+"F6.imprint","IMPRINT",FACE,{"disambiguationData":[TD([[makeQuery(id+"F6.imprint","IMPRINT",EDGE,{"derivedFrom":subQ0}),1.0]])]});}
            var Q50;
            {var subQ0=sQuery(id+"F6.wireOp",EDGE,"E8.36.0");Q50=makeQuery(id+"F6.imprint","IMPRINT",FACE,{"disambiguationData":[TD([[makeQuery(id+"F6.imprint","IMPRINT",EDGE,{"derivedFrom":subQ0}),1.0]])]});}
            var Q51;
            {var subQ0=sQuery(id+"F6.wireOp",EDGE,"E8.38.0");Q51=makeQuery(id+"F6.imprint","IMPRINT",FACE,{"disambiguationData":[TD([[makeQuery(id+"F6.imprint","IMPRINT",EDGE,{"derivedFrom":subQ0}),1.0]])]});}
            var Q52;
            {var subQ0=sQuery(id+"F6.wireOp",EDGE,"E8.81.0");Q52=makeQuery(id+"F6.imprint","IMPRINT",FACE,{"disambiguationData":[TD([[makeQuery(id+"F6.imprint","IMPRINT",EDGE,{"derivedFrom":subQ0}),1.0]])]});}
            var Q53;
            {var subQ0=sQuery(id+"F6.wireOp",EDGE,"E8.65.0");Q53=makeQuery(id+"F6.imprint","IMPRINT",FACE,{"disambiguationData":[TD([[makeQuery(id+"F6.imprint","IMPRINT",EDGE,{"derivedFrom":subQ0}),1.0]])]});}
            var Q54;
            {var subQ0=sQuery(id+"F6.wireOp",EDGE,"E8.82.0");Q54=makeQuery(id+"F6.imprint","IMPRINT",FACE,{"disambiguationData":[TD([[makeQuery(id+"F6.imprint","IMPRINT",EDGE,{"derivedFrom":subQ0}),1.0]])]});}
            var Q55;
            {var subQ0=sQuery(id+"F6.wireOp",EDGE,"E8.66.0");Q55=makeQuery(id+"F6.imprint","IMPRINT",FACE,{"disambiguationData":[TD([[makeQuery(id+"F6.imprint","IMPRINT",EDGE,{"derivedFrom":subQ0}),1.0]])]});}
            var Q56;
            {var subQ0=sQuery(id+"F6.wireOp",EDGE,"E8.14.0");Q56=makeQuery(id+"F6.imprint","IMPRINT",FACE,{"disambiguationData":[TD([[makeQuery(id+"F6.imprint","IMPRINT",EDGE,{"derivedFrom":subQ0}),1.0]])]});}
            var Q57;
            {var subQ0=sQuery(id+"F6.wireOp",EDGE,"E8.94.0");Q57=makeQuery(id+"F6.imprint","IMPRINT",FACE,{"disambiguationData":[TD([[makeQuery(id+"F6.imprint","IMPRINT",EDGE,{"derivedFrom":subQ0}),1.0]])]});}
            var Q58;
            {var subQ0=sQuery(id+"F6.wireOp",EDGE,"E8.59.0");Q58=makeQuery(id+"F6.imprint","IMPRINT",FACE,{"disambiguationData":[TD([[makeQuery(id+"F6.imprint","IMPRINT",EDGE,{"derivedFrom":subQ0}),1.0]])]});}
            var Q59;
            {var subQ0=sQuery(id+"F6.wireOp",EDGE,"E8.6.0");Q59=makeQuery(id+"F6.imprint","IMPRINT",FACE,{"disambiguationData":[TD([[makeQuery(id+"F6.imprint","IMPRINT",EDGE,{"derivedFrom":subQ0}),1.0]])]});}
            var Q60;
            {var subQ0=sQuery(id+"F6.wireOp",EDGE,"E8.93.0");Q60=makeQuery(id+"F6.imprint","IMPRINT",FACE,{"disambiguationData":[TD([[makeQuery(id+"F6.imprint","IMPRINT",EDGE,{"derivedFrom":subQ0}),1.0]])]});}
            var Q61;
            {var subQ0=sQuery(id+"F6.wireOp",EDGE,"E8.9.0");Q61=makeQuery(id+"F6.imprint","IMPRINT",FACE,{"disambiguationData":[TD([[makeQuery(id+"F6.imprint","IMPRINT",EDGE,{"derivedFrom":subQ0}),1.0]])]});}
            var Q62;
            {var subQ0=sQuery(id+"F6.wireOp",EDGE,"E8.60.0");Q62=makeQuery(id+"F6.imprint","IMPRINT",FACE,{"disambiguationData":[TD([[makeQuery(id+"F6.imprint","IMPRINT",EDGE,{"derivedFrom":subQ0}),1.0]])]});}
            var Q63;
            {var subQ0=sQuery(id+"F6.wireOp",EDGE,"E8.92.0");Q63=makeQuery(id+"F6.imprint","IMPRINT",FACE,{"disambiguationData":[TD([[makeQuery(id+"F6.imprint","IMPRINT",EDGE,{"derivedFrom":subQ0}),1.0]])]});}
            var Q64;
            {var subQ0=sQuery(id+"F6.wireOp",EDGE,"E8.44.0");Q64=makeQuery(id+"F6.imprint","IMPRINT",FACE,{"disambiguationData":[TD([[makeQuery(id+"F6.imprint","IMPRINT",EDGE,{"derivedFrom":subQ0}),1.0]])]});}
            var Q65;
            {var subQ0=sQuery(id+"F6.wireOp",EDGE,"E8.8.0");Q65=makeQuery(id+"F6.imprint","IMPRINT",FACE,{"disambiguationData":[TD([[makeQuery(id+"F6.imprint","IMPRINT",EDGE,{"derivedFrom":subQ0}),1.0]])]});}
            var Q66;
            {var subQ0=sQuery(id+"F6.wireOp",EDGE,"E8.91.0");Q66=makeQuery(id+"F6.imprint","IMPRINT",FACE,{"disambiguationData":[TD([[makeQuery(id+"F6.imprint","IMPRINT",EDGE,{"derivedFrom":subQ0}),1.0]])]});}
            var Q67;
            {var subQ0=sQuery(id+"F6.wireOp",EDGE,"E8.4.0");Q67=makeQuery(id+"F6.imprint","IMPRINT",FACE,{"disambiguationData":[TD([[makeQuery(id+"F6.imprint","IMPRINT",EDGE,{"derivedFrom":subQ0}),1.0]])]});}
            var Q68;
            {var subQ0=sQuery(id+"F6.wireOp",EDGE,"E8.68.0");Q68=makeQuery(id+"F6.imprint","IMPRINT",FACE,{"disambiguationData":[TD([[makeQuery(id+"F6.imprint","IMPRINT",EDGE,{"derivedFrom":subQ0}),1.0]])]});}
            var Q69;
            {var subQ0=sQuery(id+"F6.wireOp",EDGE,"E8.84.0");Q69=makeQuery(id+"F6.imprint","IMPRINT",FACE,{"disambiguationData":[TD([[makeQuery(id+"F6.imprint","IMPRINT",EDGE,{"derivedFrom":subQ0}),1.0]])]});}
            var Q70;
            {var subQ0=sQuery(id+"F6.wireOp",EDGE,"E8.87.0");Q70=makeQuery(id+"F6.imprint","IMPRINT",FACE,{"disambiguationData":[TD([[makeQuery(id+"F6.imprint","IMPRINT",EDGE,{"derivedFrom":subQ0}),1.0]])]});}
            var Q71;
            {var subQ0=sQuery(id+"F6.wireOp",EDGE,"E8.18.0");Q71=makeQuery(id+"F6.imprint","IMPRINT",FACE,{"disambiguationData":[TD([[makeQuery(id+"F6.imprint","IMPRINT",EDGE,{"derivedFrom":subQ0}),1.0]])]});}
            var Q72;
            {var subQ0=sQuery(id+"F6.wireOp",EDGE,"E8.63.0");Q72=makeQuery(id+"F6.imprint","IMPRINT",FACE,{"disambiguationData":[TD([[makeQuery(id+"F6.imprint","IMPRINT",EDGE,{"derivedFrom":subQ0}),1.0]])]});}
            var Q73;
            {var subQ0=sQuery(id+"F6.wireOp",EDGE,"E8.11.0");Q73=makeQuery(id+"F6.imprint","IMPRINT",FACE,{"disambiguationData":[TD([[makeQuery(id+"F6.imprint","IMPRINT",EDGE,{"derivedFrom":subQ0}),1.0]])]});}
            var Q74;
            {var subQ0=sQuery(id+"F6.wireOp",EDGE,"E8.80.0");Q74=makeQuery(id+"F6.imprint","IMPRINT",FACE,{"disambiguationData":[TD([[makeQuery(id+"F6.imprint","IMPRINT",EDGE,{"derivedFrom":subQ0}),1.0]])]});}
            var Q75;
            {var subQ0=sQuery(id+"F6.wireOp",EDGE,"E8.64.0");Q75=makeQuery(id+"F6.imprint","IMPRINT",FACE,{"disambiguationData":[TD([[makeQuery(id+"F6.imprint","IMPRINT",EDGE,{"derivedFrom":subQ0}),1.0]])]});}
            var Q76;
            {var subQ0=sQuery(id+"F6.wireOp",EDGE,"E8.41.0");Q76=makeQuery(id+"F6.imprint","IMPRINT",FACE,{"disambiguationData":[TD([[makeQuery(id+"F6.imprint","IMPRINT",EDGE,{"derivedFrom":subQ0}),1.0]])]});}
            var Q77;
            {var subQ0=sQuery(id+"F6.wireOp",EDGE,"E8.35.0");Q77=makeQuery(id+"F6.imprint","IMPRINT",FACE,{"disambiguationData":[TD([[makeQuery(id+"F6.imprint","IMPRINT",EDGE,{"derivedFrom":subQ0}),1.0]])]});}
            var Q78;
            {var subQ0=sQuery(id+"F6.wireOp",EDGE,"E8.37.0");Q78=makeQuery(id+"F6.imprint","IMPRINT",FACE,{"disambiguationData":[TD([[makeQuery(id+"F6.imprint","IMPRINT",EDGE,{"derivedFrom":subQ0}),1.0]])]});}
            var Q79;
            {var subQ0=sQuery(id+"F6.wireOp",EDGE,"E8.49.0");Q79=makeQuery(id+"F6.imprint","IMPRINT",FACE,{"disambiguationData":[TD([[makeQuery(id+"F6.imprint","IMPRINT",EDGE,{"derivedFrom":subQ0}),1.0]])]});}
            var Q80;
            {var subQ0=sQuery(id+"F6.wireOp",EDGE,"E8.57.0");Q80=makeQuery(id+"F6.imprint","IMPRINT",FACE,{"disambiguationData":[TD([[makeQuery(id+"F6.imprint","IMPRINT",EDGE,{"derivedFrom":subQ0}),1.0]])]});}
            var Q81;
            {var subQ0=sQuery(id+"F6.wireOp",EDGE,"E8.5.0");Q81=makeQuery(id+"F6.imprint","IMPRINT",FACE,{"disambiguationData":[TD([[makeQuery(id+"F6.imprint","IMPRINT",EDGE,{"derivedFrom":subQ0}),1.0]])]});}
            var Q82;
            {var subQ0=sQuery(id+"F6.wireOp",EDGE,"E8.89.0");Q82=makeQuery(id+"F6.imprint","IMPRINT",FACE,{"disambiguationData":[TD([[makeQuery(id+"F6.imprint","IMPRINT",EDGE,{"derivedFrom":subQ0}),1.0]])]});}
            var Q83;
            {var subQ0=sQuery(id+"F6.wireOp",EDGE,"E8.15.0");Q83=makeQuery(id+"F6.imprint","IMPRINT",FACE,{"disambiguationData":[TD([[makeQuery(id+"F6.imprint","IMPRINT",EDGE,{"derivedFrom":subQ0}),1.0]])]});}
            var Q84;
            {var subQ0=sQuery(id+"F6.wireOp",EDGE,"E8.16.0");Q84=makeQuery(id+"F6.imprint","IMPRINT",FACE,{"disambiguationData":[TD([[makeQuery(id+"F6.imprint","IMPRINT",EDGE,{"derivedFrom":subQ0}),1.0]])]});}
            var Q85;
            {var subQ0=sQuery(id+"F6.wireOp",EDGE,"E8.52.0");Q85=makeQuery(id+"F6.imprint","IMPRINT",FACE,{"disambiguationData":[TD([[makeQuery(id+"F6.imprint","IMPRINT",EDGE,{"derivedFrom":subQ0}),1.0]])]});}
            var Q86;
            {var subQ0=sQuery(id+"F6.wireOp",EDGE,"E8.77.0");Q86=makeQuery(id+"F6.imprint","IMPRINT",FACE,{"disambiguationData":[TD([[makeQuery(id+"F6.imprint","IMPRINT",EDGE,{"derivedFrom":subQ0}),1.0]])]});}
            var Q87;
            {var subQ0=sQuery(id+"F6.wireOp",EDGE,"E8.74.0");Q87=makeQuery(id+"F6.imprint","IMPRINT",FACE,{"disambiguationData":[TD([[makeQuery(id+"F6.imprint","IMPRINT",EDGE,{"derivedFrom":subQ0}),1.0]])]});}
            var Q88;
            {var subQ0=sQuery(id+"F6.wireOp",EDGE,"E8.76.0");Q88=makeQuery(id+"F6.imprint","IMPRINT",FACE,{"disambiguationData":[TD([[makeQuery(id+"F6.imprint","IMPRINT",EDGE,{"derivedFrom":subQ0}),1.0]])]});}
            var Q89;
            {var subQ0=sQuery(id+"F6.wireOp",EDGE,"E8.42.0");Q89=makeQuery(id+"F6.imprint","IMPRINT",FACE,{"disambiguationData":[TD([[makeQuery(id+"F6.imprint","IMPRINT",EDGE,{"derivedFrom":subQ0}),1.0]])]});}
            var Q90;
            {var subQ0=sQuery(id+"F6.wireOp",EDGE,"E8.54.0");Q90=makeQuery(id+"F6.imprint","IMPRINT",FACE,{"disambiguationData":[TD([[makeQuery(id+"F6.imprint","IMPRINT",EDGE,{"derivedFrom":subQ0}),1.0]])]});}
            var Q91;
            {var subQ0=sQuery(id+"F6.wireOp",EDGE,"E7");Q91=makeQuery(id+"F6.imprint","IMPRINT",FACE,{"disambiguationData":[TD([[makeQuery(id+"F6.imprint","IMPRINT",EDGE,{"derivedFrom":subQ0}),1.0]])]});}
            var Q92;
            {var subQ0=sQuery(id+"F6.wireOp",EDGE,"E8.3.0");Q92=makeQuery(id+"F6.imprint","IMPRINT",FACE,{"disambiguationData":[TD([[makeQuery(id+"F6.imprint","IMPRINT",EDGE,{"derivedFrom":subQ0}),1.0]])]});}
            var Q93;
            {var subQ0=sQuery(id+"F6.wireOp",EDGE,"E8.55.0");Q93=makeQuery(id+"F6.imprint","IMPRINT",FACE,{"disambiguationData":[TD([[makeQuery(id+"F6.imprint","IMPRINT",EDGE,{"derivedFrom":subQ0}),1.0]])]});}
            var Q94;
            {var subQ0=sQuery(id+"F6.wireOp",EDGE,"E8.53.0");Q94=makeQuery(id+"F6.imprint","IMPRINT",FACE,{"disambiguationData":[TD([[makeQuery(id+"F6.imprint","IMPRINT",EDGE,{"derivedFrom":subQ0}),1.0]])]});}
            var Q95;
            {var subQ0=sQuery(id+"F6.wireOp",EDGE,"E8.75.0");Q95=makeQuery(id+"F6.imprint","IMPRINT",FACE,{"disambiguationData":[TD([[makeQuery(id+"F6.imprint","IMPRINT",EDGE,{"derivedFrom":subQ0}),1.0]])]});}
            var Q96;
            {var subQ0=sQuery(id+"F6.wireOp",EDGE,"E8.39.0");Q96=makeQuery(id+"F6.imprint","IMPRINT",FACE,{"disambiguationData":[TD([[makeQuery(id+"F6.imprint","IMPRINT",EDGE,{"derivedFrom":subQ0}),1.0]])]});}
            var Q97;
            {var subQ0=sQuery(id+"F6.wireOp",EDGE,"E8.40.0");Q97=makeQuery(id+"F6.imprint","IMPRINT",FACE,{"disambiguationData":[TD([[makeQuery(id+"F6.imprint","IMPRINT",EDGE,{"derivedFrom":subQ0}),1.0]])]});}
            var Q98;
            {var subQ0=sQuery(id+"F6.wireOp",EDGE,"E8.13.0");Q98=makeQuery(id+"F6.imprint","IMPRINT",FACE,{"disambiguationData":[TD([[makeQuery(id+"F6.imprint","IMPRINT",EDGE,{"derivedFrom":subQ0}),1.0]])]});}
            var Q99;
            {var subQ0=sQuery(id+"F6.wireOp",EDGE,"E8.97.0");Q99=makeQuery(id+"F6.imprint","IMPRINT",FACE,{"disambiguationData":[TD([[makeQuery(id+"F6.imprint","IMPRINT",EDGE,{"derivedFrom":subQ0}),1.0]])]});}
            var Q100;
            {var subQ0=sQuery(id+"F6.wireOp",EDGE,"E8.50.0");Q100=makeQuery(id+"F6.imprint","IMPRINT",FACE,{"disambiguationData":[TD([[makeQuery(id+"F6.imprint","IMPRINT",EDGE,{"derivedFrom":subQ0}),1.0]])]});}
            var Q101;
            {var subQ0=sQuery(id+"F6.wireOp",EDGE,"E8.98.0");Q101=makeQuery(id+"F6.imprint","IMPRINT",FACE,{"disambiguationData":[TD([[makeQuery(id+"F6.imprint","IMPRINT",EDGE,{"derivedFrom":subQ0}),1.0]])]});}
            var Q102;
            {var subQ0=sQuery(id+"F6.wireOp",EDGE,"E8.83.0");Q102=makeQuery(id+"F6.imprint","IMPRINT",FACE,{"disambiguationData":[TD([[makeQuery(id+"F6.imprint","IMPRINT",EDGE,{"derivedFrom":subQ0}),1.0]])]});}
            var Q103;
            {var subQ0=sQuery(id+"F6.wireOp",EDGE,"E8.67.0");Q103=makeQuery(id+"F6.imprint","IMPRINT",FACE,{"disambiguationData":[TD([[makeQuery(id+"F6.imprint","IMPRINT",EDGE,{"derivedFrom":subQ0}),1.0]])]});}
            var Q104;
            {var subQ0=sQuery(id+"F6.wireOp",EDGE,"E8.51.0");Q104=makeQuery(id+"F6.imprint","IMPRINT",FACE,{"disambiguationData":[TD([[makeQuery(id+"F6.imprint","IMPRINT",EDGE,{"derivedFrom":subQ0}),1.0]])]});}
            var Q105;
            {var subQ0=sQuery(id+"F6.wireOp",EDGE,"E8.99.0");Q105=makeQuery(id+"F6.imprint","IMPRINT",FACE,{"disambiguationData":[TD([[makeQuery(id+"F6.imprint","IMPRINT",EDGE,{"derivedFrom":subQ0}),1.0]])]});}
            var Q106;
            {var subQ0=sQuery(id+"F6.wireOp",EDGE,"E8.46.0");Q106=makeQuery(id+"F6.imprint","IMPRINT",FACE,{"disambiguationData":[TD([[makeQuery(id+"F6.imprint","IMPRINT",EDGE,{"derivedFrom":subQ0}),1.0]])]});}
            var Q107;
            {var subQ0=sQuery(id+"F6.wireOp",EDGE,"E8.1.0");Q107=makeQuery(id+"F6.imprint","IMPRINT",FACE,{"disambiguationData":[TD([[makeQuery(id+"F6.imprint","IMPRINT",EDGE,{"derivedFrom":subQ0}),1.0]])]});}
            var Q108;
            {var subQ0=sQuery(id+"F6.wireOp",EDGE,"E8.2.0");Q108=makeQuery(id+"F6.imprint","IMPRINT",FACE,{"disambiguationData":[TD([[makeQuery(id+"F6.imprint","IMPRINT",EDGE,{"derivedFrom":subQ0}),1.0]])]});}
            var Q109;
            {var subQ0=sQuery(id+"F6.wireOp",EDGE,"E8.62.0");Q109=makeQuery(id+"F6.imprint","IMPRINT",FACE,{"disambiguationData":[TD([[makeQuery(id+"F6.imprint","IMPRINT",EDGE,{"derivedFrom":subQ0}),1.0]])]});}
            var Q110;
            {var subQ0=sQuery(id+"F6.wireOp",EDGE,"E8.73.0");Q110=makeQuery(id+"F6.imprint","IMPRINT",FACE,{"disambiguationData":[TD([[makeQuery(id+"F6.imprint","IMPRINT",EDGE,{"derivedFrom":subQ0}),1.0]])]});}
            var Q111;
            {var subQ0=sQuery(id+"F6.wireOp",EDGE,"E8.30.0");Q111=makeQuery(id+"F6.imprint","IMPRINT",FACE,{"disambiguationData":[TD([[makeQuery(id+"F6.imprint","IMPRINT",EDGE,{"derivedFrom":subQ0}),1.0]])]});}
            var Q112;
            {var subQ0=sQuery(id+"F6.wireOp",EDGE,"E9.2.70.0");Q112=makeQuery(id+"F6.imprint","IMPRINT",FACE,{"disambiguationData":[TD([[makeQuery(id+"F6.imprint","IMPRINT",EDGE,{"derivedFrom":subQ0}),1.0]])]});}
            var Q113;
            {var subQ0=sQuery(id+"F6.wireOp",EDGE,"E9.2.71.0");Q113=makeQuery(id+"F6.imprint","IMPRINT",FACE,{"disambiguationData":[TD([[makeQuery(id+"F6.imprint","IMPRINT",EDGE,{"derivedFrom":subQ0}),1.0]])]});}
            var Q114;
            {var subQ0=sQuery(id+"F6.wireOp",EDGE,"E9.2.72.0");Q114=makeQuery(id+"F6.imprint","IMPRINT",FACE,{"disambiguationData":[TD([[makeQuery(id+"F6.imprint","IMPRINT",EDGE,{"derivedFrom":subQ0}),1.0]])]});}
            var Q115;
            {var subQ0=sQuery(id+"F6.wireOp",EDGE,"E9.2.73.0");Q115=makeQuery(id+"F6.imprint","IMPRINT",FACE,{"disambiguationData":[TD([[makeQuery(id+"F6.imprint","IMPRINT",EDGE,{"derivedFrom":subQ0}),1.0]])]});}
            var Q116;
            {var subQ0=sQuery(id+"F6.wireOp",EDGE,"E9.2.74.0");Q116=makeQuery(id+"F6.imprint","IMPRINT",FACE,{"disambiguationData":[TD([[makeQuery(id+"F6.imprint","IMPRINT",EDGE,{"derivedFrom":subQ0}),1.0]])]});}
            var Q117;
            {var subQ2=sQuery(id+"F6.wireOp",EDGE,"E0.rect.top");Q117=makeQuery(id+"F6.imprint","IMPRINT",FACE,{"disambiguationData":[TD([[makeQuery(id+"F6.imprint","IMPRINT",EDGE,{"derivedFrom":subQ2}),-1.0]])]});}
            var Q118;
            {var subQ4=sQuery(id+"F6.wireOp",EDGE,"E5.3.0");Q118=makeQuery(id+"F6.imprint","IMPRINT",FACE,{"disambiguationData":[TD([[makeQuery(id+"F6.imprint","IMPRINT",EDGE,{"derivedFrom":subQ4}),-1.0]])]});}
            var Q119;
            {var subQ1=sQuery(id+"F6.wireOp",EDGE,"E10.MirrorCS");Q119=makeQuery(id+"F6.imprint","IMPRINT",FACE,{"disambiguationData":[TD([[makeQuery(id+"F6.imprint","IMPRINT",EDGE,{"derivedFrom":subQ1}),1.0]])]});}
            var Q120;
            {var subQ5=sQuery(id+"F6.wireOp",EDGE,"E11.MirrorCS");Q120=makeQuery(id+"F6.imprint","IMPRINT",FACE,{"disambiguationData":[TD([[makeQuery(id+"F6.imprint","IMPRINT",EDGE,{"derivedFrom":subQ5}),1.0]])]});}
            var Q121;
            {var subQ1=sQuery(id+"F6.wireOp",EDGE,"E12.MirrorCS");Q121=makeQuery(id+"F6.imprint","IMPRINT",FACE,{"disambiguationData":[TD([[makeQuery(id+"F6.imprint","IMPRINT",EDGE,{"derivedFrom":subQ1}),-1.0]])]});}
            var Q122;
            {var subQ4=sQuery(id+"F6.wireOp",EDGE,"E5.3.1");Q122=makeQuery(id+"F6.imprint","IMPRINT",FACE,{"disambiguationData":[TD([[makeQuery(id+"F6.imprint","IMPRINT",EDGE,{"derivedFrom":subQ4}),1.0]])]});}
            var Q123;
            {var subQ4=sQuery(id+"F6.wireOp",EDGE,"E10.MirrorCS");Q123=makeQuery(id+"F6.imprint","IMPRINT",FACE,{"disambiguationData":[TD([[makeQuery(id+"F6.imprint","IMPRINT",EDGE,{"derivedFrom":subQ4}),-1.0]])]});}
            var Q124;
            Q124=makeQuery(id+"F6.imprint","IMPRINT",FACE,{"disambiguationData":[TD([[makeQuery(id+"F6.imprint","IMPRINT",EDGE,{"derivedFrom":sQuery(id+"F6.wireOp",EDGE,"E1")}),1.0]])]});
            extrude(context, id + "F9", {"entities" : qUnion([Q0, Q1, Q2, Q3, Q4, Q5, Q6, Q7, Q8, Q9, Q10, Q11, Q12, Q13, Q14, Q15, Q16, Q17, Q18, Q19, Q20, Q21, Q22, Q23, Q24, Q25, Q26, Q27, Q28, Q29, Q30, Q31, Q32, Q33, Q34, Q35, Q36, Q37, Q38, Q39, Q40, Q41, Q42, Q43, Q44, Q45, Q46, Q47, Q48, Q49, Q50, Q51, Q52, Q53, Q54, Q55, Q56, Q57, Q58, Q59, Q60, Q61, Q62, Q63, Q64, Q65, Q66, Q67, Q68, Q69, Q70, Q71, Q72, Q73, Q74, Q75, Q76, Q77, Q78, Q79, Q80, Q81, Q82, Q83, Q84, Q85, Q86, Q87, Q88, Q89, Q90, Q91, Q92, Q93, Q94, Q95, Q96, Q97, Q98, Q99, Q100, Q101, Q102, Q103, Q104, Q105, Q106, Q107, Q108, Q109, Q110, Q111, Q112, Q113, Q114, Q115, Q116, Q117, Q118, Q119, Q120, Q121, Q122, Q123, Q124]), "operationType" : NewBodyOperationType.ADD, "oppositeDirection" : true, "depth" : (getVariable(context, 'WallThickness')) * mm});
        }
        {
            var Q0;
            {var subQ1=sQuery(id+"F6.wireOp",EDGE,"E5.3.0");Q0=makeQuery(id+"F6.imprint","IMPRINT",FACE,{"disambiguationData":[TD([[makeQuery(id+"F6.imprint","IMPRINT",EDGE,{"derivedFrom":subQ1}),1.0]])]});}
            var Q1;
            {var subQ1=sQuery(id+"F6.wireOp",EDGE,"E10.MirrorCS");Q1=makeQuery(id+"F6.imprint","IMPRINT",FACE,{"disambiguationData":[TD([[makeQuery(id+"F6.imprint","IMPRINT",EDGE,{"derivedFrom":subQ1}),1.0]])]});}
            var Q2;
            {var subQ1=sQuery(id+"F6.wireOp",EDGE,"E12.MirrorCS");Q2=makeQuery(id+"F6.imprint","IMPRINT",FACE,{"disambiguationData":[TD([[makeQuery(id+"F6.imprint","IMPRINT",EDGE,{"derivedFrom":subQ1}),-1.0]])]});}
            var Q3;
            {var subQ1=sQuery(id+"F6.wireOp",EDGE,"E14.MirrorCS");Q3=makeQuery(id+"F6.imprint","IMPRINT",FACE,{"disambiguationData":[TD([[makeQuery(id+"F6.imprint","IMPRINT",EDGE,{"derivedFrom":subQ1}),1.0]])]});}
            extrude(context, id + "F10", {"entities" : qUnion([Q0, Q1, Q2, Q3]), "operationType" : NewBodyOperationType.ADD, "depth" : (getVariable(context, 'CylinderHeight')) * mm});
        }
        {
            var Q0;
            Q0=makeQuery(id+"F10.opExtrude","CAP_EDGE",EDGE,{"disambiguationData":[OSD([sQuery(id+"F6.wireOp",EDGE,"E0.rect.right")])],"isStart":false});
            var Q1;
            Q1=makeQuery(id+"F10.opExtrude","CAP_EDGE",EDGE,{"disambiguationData":[OSD([sQuery(id+"F6.wireOp",EDGE,"E0.rect.top")])],"isStart":false});
            var Q2;
            Q2=makeQuery(id+"F10.opExtrude","CAP_EDGE",EDGE,{"disambiguationData":[OSD([sQuery(id+"F6.wireOp",EDGE,"E0.rect.left")])],"isStart":false});
            var Q3;
            Q3=makeQuery(id+"F10.opExtrude","CAP_EDGE",EDGE,{"disambiguationData":[OSD([sQuery(id+"F6.wireOp",EDGE,"E0.rect.bottom")])],"isStart":false});
            chamfer(context, id + "F11", {"entities" : qUnion([Q0, Q1, Q2, Q3]), "chamferType" : ChamferType.TWO_OFFSETS, "width1" : (getVariable(context, 'PlateWidth') - getVariable(context, 'TableLegDiameter') - (getVariable(context, 'WallThickness') * 2)) / 2 * mm, "oppositeDirection" : false, "width2" : (getVariable(context, 'CylinderHeight')) * mm, "tangentPropagation" : true});
        }
        {
            var Q0;
            Q0=sQuery(id+"F6.wireOp",VERTEX,"E16.MirrorP");
            var Q1;
            Q1=sQuery(id+"F6.wireOp",VERTEX,"E6");
            var Q2;
            Q2=sQuery(id+"F6.wireOp",VERTEX,"E17.MirrorP");
            var Q3;
            Q3=sQuery(id+"F6.wireOp",VERTEX,"E18.MirrorP");
            var Q4;
            Q4=makeQuery(id+"F8.opExtrude","SWEPT_BODY",BODY,{"disambiguationData":[OSD([sQuery(id+"F6.wireOp",EDGE,"E1"),sQuery(id+"F6.wireOp",EDGE,"E4.0")])]});
            hole(context, id + "F12", {"style" : HoleStyle.SIMPLE, "holeDiameter" : (getVariable(context, 'BoltHoleDiameter')) * mm, "endStyle" : HoleEndStyle.THROUGH, "locations" : qUnion([Q0, Q1, Q2, Q3]), "scope" : qUnion([Q4])});
        }
        {
            var Q0;
            Q0=makeQuery(id+"F10.opExtrude","CAP_EDGE",EDGE,{"disambiguationData":[OSD([sQuery(id+"F6.wireOp",EDGE,"E12.MirrorCS")])],"isStart":true});
            var Q1;
            {var subQ0=sQuery(id+"F6.wireOp",EDGE,"E4.0");Q1=makeQuery(id+"F10.boolean.opBoolean","SPLIT",EDGE,{"disambiguationData":[TD([makeQuery(id+"F10.opExtrude","SWEPT_FACE",FACE,{"disambiguationData":[OSD([sQuery(id+"F6.wireOp",EDGE,"E5.3.0")])]})])],"derivedFrom":makeQuery(id+"F8.opExtrude","CAP_EDGE",EDGE,{"disambiguationData":[OSD([subQ0])],"isStart":true})});}
            var Q2;
            Q2=makeQuery(id+"F10.opExtrude","CAP_EDGE",EDGE,{"disambiguationData":[OSD([sQuery(id+"F6.wireOp",EDGE,"E5.3.0")])],"isStart":true});
            var Q3;
            Q3=makeQuery(id+"F10.opExtrude","CAP_EDGE",EDGE,{"disambiguationData":[OSD([sQuery(id+"F6.wireOp",EDGE,"E5.3.1")])],"isStart":true});
            var Q4;
            {var subQ0=sQuery(id+"F6.wireOp",EDGE,"E4.0");Q4=makeQuery(id+"F10.boolean.opBoolean","SPLIT",EDGE,{"disambiguationData":[TD([makeQuery(id+"F10.opExtrude","SWEPT_FACE",FACE,{"disambiguationData":[OSD([sQuery(id+"F6.wireOp",EDGE,"E5.3.1")])]})])],"derivedFrom":makeQuery(id+"F8.opExtrude","CAP_EDGE",EDGE,{"disambiguationData":[OSD([subQ0])],"isStart":true})});}
            var Q5;
            Q5=makeQuery(id+"F10.opExtrude","CAP_EDGE",EDGE,{"disambiguationData":[OSD([sQuery(id+"F6.wireOp",EDGE,"E14.MirrorCS")])],"isStart":true});
            var Q6;
            Q6=makeQuery(id+"F10.opExtrude","CAP_EDGE",EDGE,{"disambiguationData":[OSD([sQuery(id+"F6.wireOp",EDGE,"E15.MirrorCS")])],"isStart":true});
            var Q7;
            {var subQ0=sQuery(id+"F6.wireOp",EDGE,"E4.0");Q7=makeQuery(id+"F10.boolean.opBoolean","SPLIT",EDGE,{"disambiguationData":[TD([makeQuery(id+"F10.opExtrude","SWEPT_FACE",FACE,{"disambiguationData":[OSD([sQuery(id+"F6.wireOp",EDGE,"E10.MirrorCS")])]})])],"derivedFrom":makeQuery(id+"F8.opExtrude","CAP_EDGE",EDGE,{"disambiguationData":[OSD([subQ0])],"isStart":true})});}
            var Q8;
            Q8=makeQuery(id+"F10.opExtrude","CAP_EDGE",EDGE,{"disambiguationData":[OSD([sQuery(id+"F6.wireOp",EDGE,"E10.MirrorCS")])],"isStart":true});
            var Q9;
            Q9=makeQuery(id+"F10.opExtrude","CAP_EDGE",EDGE,{"disambiguationData":[OSD([sQuery(id+"F6.wireOp",EDGE,"E11.MirrorCS")])],"isStart":true});
            var Q10;
            {var subQ0=sQuery(id+"F6.wireOp",EDGE,"E4.0");Q10=makeQuery(id+"F10.boolean.opBoolean","SPLIT",EDGE,{"disambiguationData":[TD([makeQuery(id+"F10.opExtrude","SWEPT_FACE",FACE,{"disambiguationData":[OSD([sQuery(id+"F6.wireOp",EDGE,"E11.MirrorCS")])]})])],"derivedFrom":makeQuery(id+"F8.opExtrude","CAP_EDGE",EDGE,{"disambiguationData":[OSD([subQ0])],"isStart":true})});}
            var Q11;
            Q11=makeQuery(id+"F10.opExtrude","CAP_EDGE",EDGE,{"disambiguationData":[OSD([sQuery(id+"F6.wireOp",EDGE,"E13.MirrorCS")])],"isStart":true});
            chamfer(context, id + "F13", {"entities" : qUnion([Q0, Q1, Q2, Q3, Q4, Q5, Q6, Q7, Q8, Q9, Q10, Q11]), "width" : 6 * mm, "tangentPropagation" : true});
        }
    });
